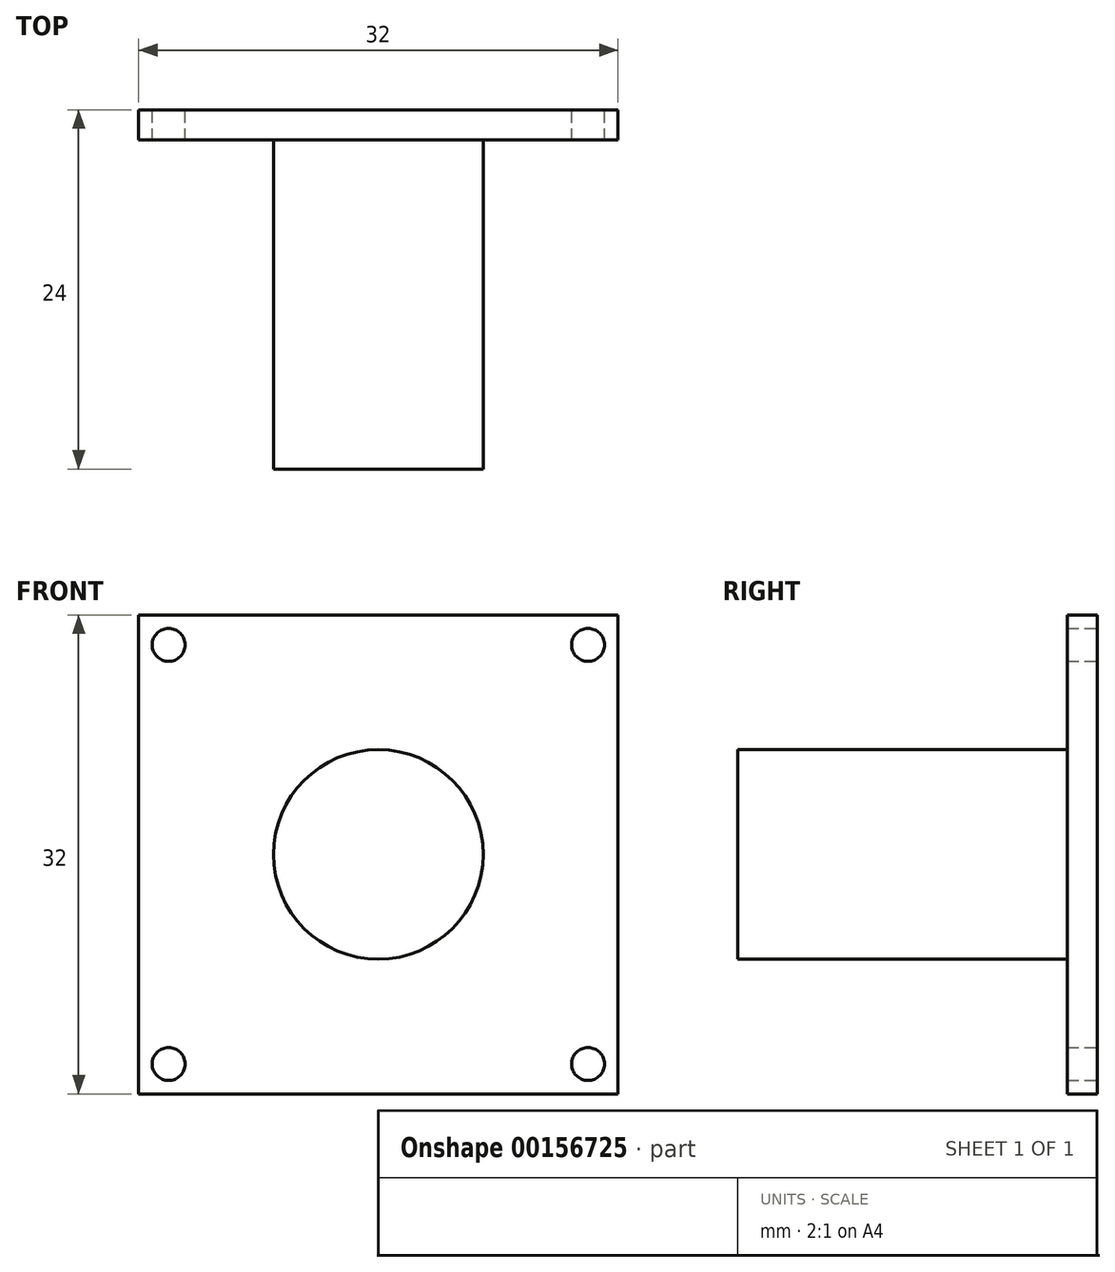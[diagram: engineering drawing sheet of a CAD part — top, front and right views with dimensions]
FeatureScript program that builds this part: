
annotation { "Feature Type Name" : "Feature", "Feature Type Description" : "" }
export const myFeature = defineFeature(function(context is Context, id is Id, definition is map)
    precondition{}
    {
        {
            var Q0;
            Q0=qCreatedBy(makeId("Front.planeOp"),FACE);
            var sketch = newSketch(context, id + "F0", { "sketchPlane" : qUnion([Q0])});
            skLineSegment(sketch, "E0.bottom", {"start": v(16, -16) * mm, "end": v(-16, -16) * mm});
            skLineSegment(sketch, "E0.top", {"start": v(16, 16) * mm, "end": v(-16, 16) * mm});
            skLineSegment(sketch, "E0.left", {"start": v(16, -16) * mm, "end": v(16, 16) * mm});
            skLineSegment(sketch, "E0.right", {"start": v(-16, -16) * mm, "end": v(-16, 16) * mm});
            skPoint(sketch, "E0.middle", {"position": v(0, 0) * mm});
            skCircle(sketch, "E1", {"center": v(0, 0) * mm, "radius": 7 * mm});
            skCircle(sketch, "E2", {"center": v(-14, 14) * mm, "radius": 1.1 * mm});
            skCircle(sketch, "E3.MirrorC", {"center": v(14, 14) * mm, "radius": 1.1 * mm});
            skCircle(sketch, "E4.MirrorC", {"center": v(14, -14) * mm, "radius": 1.1 * mm});
            skCircle(sketch, "E5.MirrorC", {"center": v(-14, -14) * mm, "radius": 1.1 * mm});
            skSolve(sketch);
        }
        {
            var Q0;
            Q0=makeQuery(id+"F0.imprint","IMPRINT",FACE,{"disambiguationData":[TD([[makeQuery(id+"F0.imprint","IMPRINT",EDGE,{"derivedFrom":sQuery(id+"F0.wireOp",EDGE,"E0.bottom")}),-1.0]])]});
            var Q1;
            Q1=makeQuery(id+"F0.imprint","IMPRINT",FACE,{"disambiguationData":[TD([[makeQuery(id+"F0.imprint","IMPRINT",EDGE,{"derivedFrom":sQuery(id+"F0.wireOp",EDGE,"E1")}),1.0]])]});
            extrude(context, id + "F1", {"entities" : qUnion([Q0, Q1]), "depth" : 2 * mm});
        }
        {
            var Q0;
            Q0=makeQuery(id+"F0.imprint","IMPRINT",FACE,{"disambiguationData":[TD([[makeQuery(id+"F0.imprint","IMPRINT",EDGE,{"derivedFrom":sQuery(id+"F0.wireOp",EDGE,"E1")}),1.0]])]});
            var Q1;
            Q1=sQuery(id+"F0.wireOp",EDGE,"E1");
            extrude(context, id + "F2", {"entities" : qUnion([Q0]), "operationType" : NewBodyOperationType.ADD, "surfaceEntities" : qUnion([Q1]), "depth" : 24 * mm});
        }
    });
